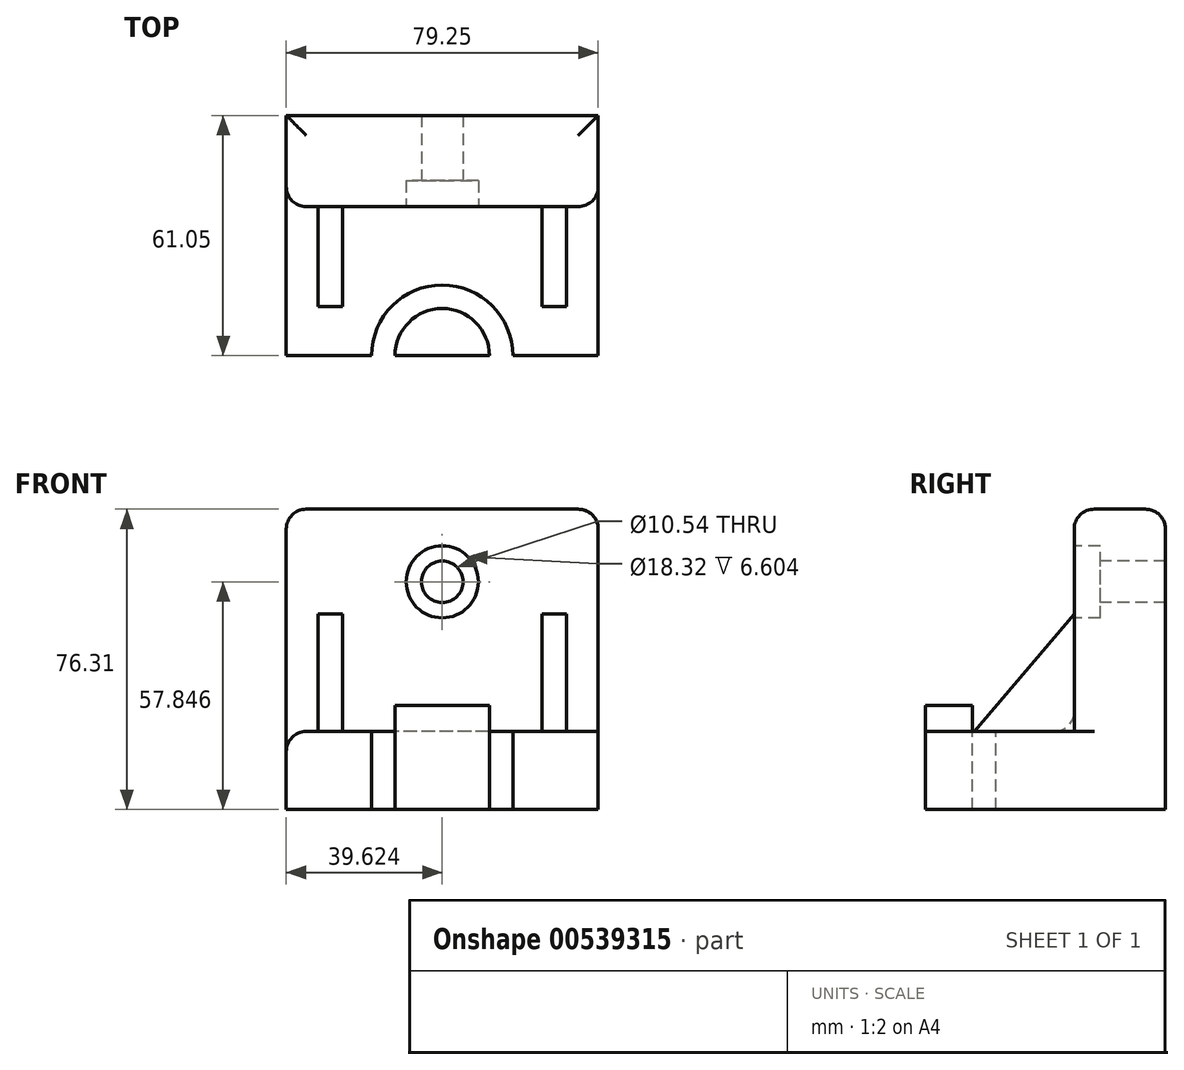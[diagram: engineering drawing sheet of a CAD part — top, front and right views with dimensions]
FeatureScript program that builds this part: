
annotation { "Feature Type Name" : "Feature", "Feature Type Description" : "" }
export const myFeature = defineFeature(function(context is Context, id is Id, definition is map)
    precondition{}
    {
        {
            var Q0;
            Q0=qCreatedBy(makeId("Right.planeOp"),FACE);
            var sketch = newSketch(context, id + "F0", { "sketchPlane" : qUnion([Q0])});
            skLineSegment(sketch, "E0", {"start": v(10.38, 56.47) * mm, "end": v(33.58, 56.47) * mm});
            skLineSegment(sketch, "E1", {"start": v(33.58, 56.47) * mm, "end": v(33.58, -19.84) * mm});
            skLineSegment(sketch, "E2", {"start": v(33.58, -19.84) * mm, "end": v(-27.47, -19.84) * mm});
            skLineSegment(sketch, "E3", {"start": v(-27.47, -19.84) * mm, "end": v(-27.47, 0) * mm});
            skLineSegment(sketch, "E4", {"start": v(-27.47, 0) * mm, "end": v(10.38, 0) * mm});
            skLineSegment(sketch, "E5", {"start": v(10.38, 0) * mm, "end": v(10.38, 56.47) * mm});
            skSolve(sketch);
        }
        {
            var Q0;
            Q0 = qSketchRegion(id + "F0", true);
            var Q1;
            Q1=makeQuery(id+"F0.imprint","IMPRINT",FACE,{"disambiguationData":[TD([[makeQuery(id+"F0.imprint","IMPRINT",EDGE,{"derivedFrom":sQuery(id+"F0.wireOp",EDGE,"E0")}),-1.0]])]});
            extrude(context, id + "F1", {"entities" : qUnion([Q0, Q1]), "depth" : 79.25 * mm, "offsetDistance" : 25.4 * mm});
        }
        {
            var Q0;
            Q0=makeQuery(id+"F1.opExtrude","SWEPT_FACE",FACE,{"disambiguationData":[OSD([sQuery(id+"F0.wireOp",EDGE,"E5")])]});
            var sketch = newSketch(context, id + "F2", { "sketchPlane" : qUnion([Q0])});
            skCircle(sketch, "E6", {"center": v(39.62, 38) * mm, "radius": 9.16 * mm});
            skPoint(sketch, "E6.centerSnap0", {"position": v(39.62, 56.47) * mm});
            skCircle(sketch, "E7", {"center": v(39.62, 38) * mm, "radius": 5.27 * mm});
            skLineSegment(sketch, "E8.bottom", {"start": v(8.04, 0) * mm, "end": v(14.3, 0) * mm});
            skLineSegment(sketch, "E8.top", {"start": v(8.04, 29.8) * mm, "end": v(14.3, 29.8) * mm});
            skLineSegment(sketch, "E8.left", {"start": v(8.04, 0) * mm, "end": v(8.04, 29.8) * mm});
            skLineSegment(sketch, "E8.right", {"start": v(14.3, 0) * mm, "end": v(14.3, 29.8) * mm});
            skLineSegment(sketch, "E9", {"start": v(39.62, 56.47) * mm, "end": v(39.62, 0) * mm, "construction": true});
            skLineSegment(sketch, "E10.MirrorCS", {"start": v(71.21, 0) * mm, "end": v(64.94, 0) * mm});
            skLineSegment(sketch, "E11.MirrorCS", {"start": v(71.21, 29.8) * mm, "end": v(64.94, 29.8) * mm});
            skLineSegment(sketch, "E12.MirrorCS", {"start": v(71.21, 0) * mm, "end": v(71.21, 29.8) * mm});
            skLineSegment(sketch, "E13.MirrorCS", {"start": v(64.94, 0) * mm, "end": v(64.94, 29.8) * mm});
            skSolve(sketch);
        }
        {
            var Q0;
            Q0=makeQuery(id+"F2.imprint","IMPRINT",FACE,{"disambiguationData":[TD([[makeQuery(id+"F2.imprint","IMPRINT",EDGE,{"derivedFrom":sQuery(id+"F2.wireOp",EDGE,"E8.bottom")}),-1.0]])]});
            extrude(context, id + "F3", {"entities" : qUnion([Q0]), "operationType" : NewBodyOperationType.ADD, "depth" : 25.4 * mm, "offsetDistance" : 25.4 * mm});
        }
        {
            var Q0;
            Q0=makeQuery(id+"F2.imprint","IMPRINT",FACE,{"disambiguationData":[TD([[makeQuery(id+"F2.imprint","IMPRINT",EDGE,{"derivedFrom":sQuery(id+"F2.wireOp",EDGE,"E10.MirrorCS")}),-1.0]])]});
            extrude(context, id + "F4", {"entities" : qUnion([Q0]), "operationType" : NewBodyOperationType.ADD, "depth" : 25.4 * mm, "offsetDistance" : 25.4 * mm});
        }
        {
            var Q0;
            Q0=makeQuery(id+"F1.opExtrude","SWEPT_FACE",FACE,{"disambiguationData":[OSD([sQuery(id+"F0.wireOp",EDGE,"E4")])]});
            var sketch = newSketch(context, id + "F5", { "sketchPlane" : qUnion([Q0])});
            skArc(sketch, "E14", {"start": v(27.64, -27.47) * mm, "mid": v(39.62, -15.49) * mm, "end": v(51.61, -27.47) * mm});
            skArc(sketch, "E15", {"start": v(21.7, -27.47) * mm, "mid": v(39.62, -9.55) * mm, "end": v(57.55, -27.47) * mm});
            skSolve(sketch);
        }
        {
            var Q0;
            {var subQ0=sQuery(id+"F5.wireOp",EDGE,"E14");Q0=makeQuery(id+"F5.imprint","IMPRINT",FACE,{"disambiguationData":[TD([[makeQuery(id+"F5.imprint","IMPRINT",EDGE,{"derivedFrom":subQ0}),-1.0]])]});}
            extrude(context, id + "F6", {"entities" : qUnion([Q0]), "operationType" : NewBodyOperationType.REMOVE, "oppositeDirection" : true, "depth" : 25.4 * mm, "offsetDistance" : 25.4 * mm});
        }
        {
            var Q0;
            {var subQ0=sQuery(id+"F5.wireOp",EDGE,"E14");Q0=makeQuery(id+"F5.imprint","IMPRINT",FACE,{"disambiguationData":[TD([[makeQuery(id+"F5.imprint","IMPRINT",EDGE,{"derivedFrom":subQ0}),1.0]])]});}
            extrude(context, id + "F7", {"entities" : qUnion([Q0]), "operationType" : NewBodyOperationType.ADD, "depth" : 6.6 * mm, "offsetDistance" : 25.4 * mm});
        }
        {
            var Q0;
            Q0=makeQuery(id+"F4.opExtrude","SWEPT_FACE",FACE,{"disambiguationData":[OSD([sQuery(id+"F2.wireOp",EDGE,"E12.MirrorCS")])]});
            var sketch = newSketch(context, id + "F8", { "sketchPlane" : qUnion([Q0])});
            skLineSegment(sketch, "E16", {"start": v(10.38, 29.8) * mm, "end": v(-15.02, 0) * mm});
            skSolve(sketch);
        }
        {
            var Q0;
            Q0=makeQuery(id+"F8.imprint","IMPRINT",FACE,{"disambiguationData":[TD([[makeQuery(id+"F8.imprint","IMPRINT",EDGE,{"derivedFrom":sQuery(id+"F8.wireOp",EDGE,"E16")}),-1.0]])]});
            extrude(context, id + "F9", {"entities" : qUnion([Q0]), "operationType" : NewBodyOperationType.REMOVE, "oppositeDirection" : true, "depth" : 25.4 * mm, "offsetDistance" : 25.4 * mm});
        }
        {
            var Q0;
            Q0=makeQuery(id+"F3.opExtrude","SWEPT_FACE",FACE,{"disambiguationData":[OSD([sQuery(id+"F2.wireOp",EDGE,"E8.left")])]});
            var sketch = newSketch(context, id + "F10", { "sketchPlane" : qUnion([Q0])});
            skLineSegment(sketch, "E17", {"start": v(-10.38, 29.8) * mm, "end": v(15.02, 0) * mm});
            skSolve(sketch);
        }
        {
            var Q0;
            Q0=makeQuery(id+"F10.imprint","IMPRINT",FACE,{"disambiguationData":[TD([[makeQuery(id+"F10.imprint","IMPRINT",EDGE,{"derivedFrom":sQuery(id+"F10.wireOp",EDGE,"E17")}),1.0]])]});
            extrude(context, id + "F11", {"entities" : qUnion([Q0]), "operationType" : NewBodyOperationType.REMOVE, "oppositeDirection" : true, "depth" : 25.4 * mm, "offsetDistance" : 25.4 * mm});
        }
        {
            var Q0;
            Q0=makeQuery(id+"F2.imprint","IMPRINT",FACE,{"disambiguationData":[TD([[makeQuery(id+"F2.imprint","IMPRINT",EDGE,{"derivedFrom":sQuery(id+"F2.wireOp",EDGE,"E7")}),1.0]])]});
            var Q1;
            Q1=sQuery(id+"F2.wireOp",EDGE,"E7");
            extrude(context, id + "F12", {"entities" : qUnion([Q0]), "operationType" : NewBodyOperationType.REMOVE, "surfaceEntities" : qUnion([Q1]), "oppositeDirection" : true, "depth" : 25.4 * mm, "offsetDistance" : 25.4 * mm});
        }
        {
            var Q0;
            Q0=makeQuery(id+"F2.imprint","IMPRINT",FACE,{"disambiguationData":[TD([[makeQuery(id+"F2.imprint","IMPRINT",EDGE,{"derivedFrom":sQuery(id+"F2.wireOp",EDGE,"E6")}),1.0]])]});
            extrude(context, id + "F13", {"entities" : qUnion([Q0]), "operationType" : NewBodyOperationType.REMOVE, "oppositeDirection" : true, "depth" : 6.6 * mm, "offsetDistance" : 25.4 * mm});
        }
        {
            var Q0;
            Q0=makeQuery(id+"F1.opExtrude","CAP_EDGE",EDGE,{"disambiguationData":[OSD([sQuery(id+"F0.wireOp",EDGE,"E0")])],"isStart":true});
            var Q1;
            Q1=makeQuery(id+"F1.opExtrude","CAP_EDGE",EDGE,{"disambiguationData":[OSD([sQuery(id+"F0.wireOp",EDGE,"E0")])],"isStart":false});
            var Q2;
            Q2=makeQuery(id+"F1.opExtrude","CAP_EDGE",EDGE,{"disambiguationData":[OSD([sQuery(id+"F0.wireOp",EDGE,"E4")])],"isStart":true});
            var Q3;
            Q3=makeQuery(id+"F1.opExtrude","CAP_EDGE",EDGE,{"disambiguationData":[OSD([sQuery(id+"F0.wireOp",EDGE,"E5")])],"isStart":true});
            var Q4;
            Q4=makeQuery(id+"F1.opExtrude","SWEPT_EDGE",EDGE,{"disambiguationData":[OSD([sQuery(id+"F0.wireOp",EDGE,"E0"),sQuery(id+"F0.wireOp",EDGE,"E5")])]});
            var Q5;
            Q5=makeQuery(id+"F1.opExtrude","SWEPT_EDGE",EDGE,{"disambiguationData":[OSD([sQuery(id+"F0.wireOp",EDGE,"E0"),sQuery(id+"F0.wireOp",EDGE,"E1")])]});
            var Q6;
            Q6=makeQuery(id+"F1.opExtrude","CAP_EDGE",EDGE,{"disambiguationData":[OSD([sQuery(id+"F0.wireOp",EDGE,"E5")])],"isStart":false});
            var Q7;
            {var subQ0=sQuery(id+"F0.wireOp",EDGE,"E4");var subQ2=sQuery(id+"F0.wireOp",EDGE,"E5");var subQ4=makeQuery(id+"F3.opExtrude","SWEPT_FACE",FACE,{"disambiguationData":[OSD([sQuery(id+"F2.wireOp",EDGE,"E8.right")])]});Q7=makeQuery(id+"F4.boolean.opBoolean","SPLIT",EDGE,{"disambiguationData":[TD([subQ4])],"derivedFrom":makeQuery(id+"F3.boolean.opBoolean","SPLIT",EDGE,{"disambiguationData":[TD([subQ4])],"derivedFrom":makeQuery(id+"F1.opExtrude","SWEPT_EDGE",EDGE,{"disambiguationData":[OSD([subQ0,subQ2])]})})});}
            fillet(context, id + "F14", {"entities" : qUnion([Q0, Q1, Q2, Q3, Q4, Q5, Q6, Q7]), "radius" : 5.08 * mm, "tangentPropagation" : true, "allowEdgeOverflow" : false});
        }
    });
